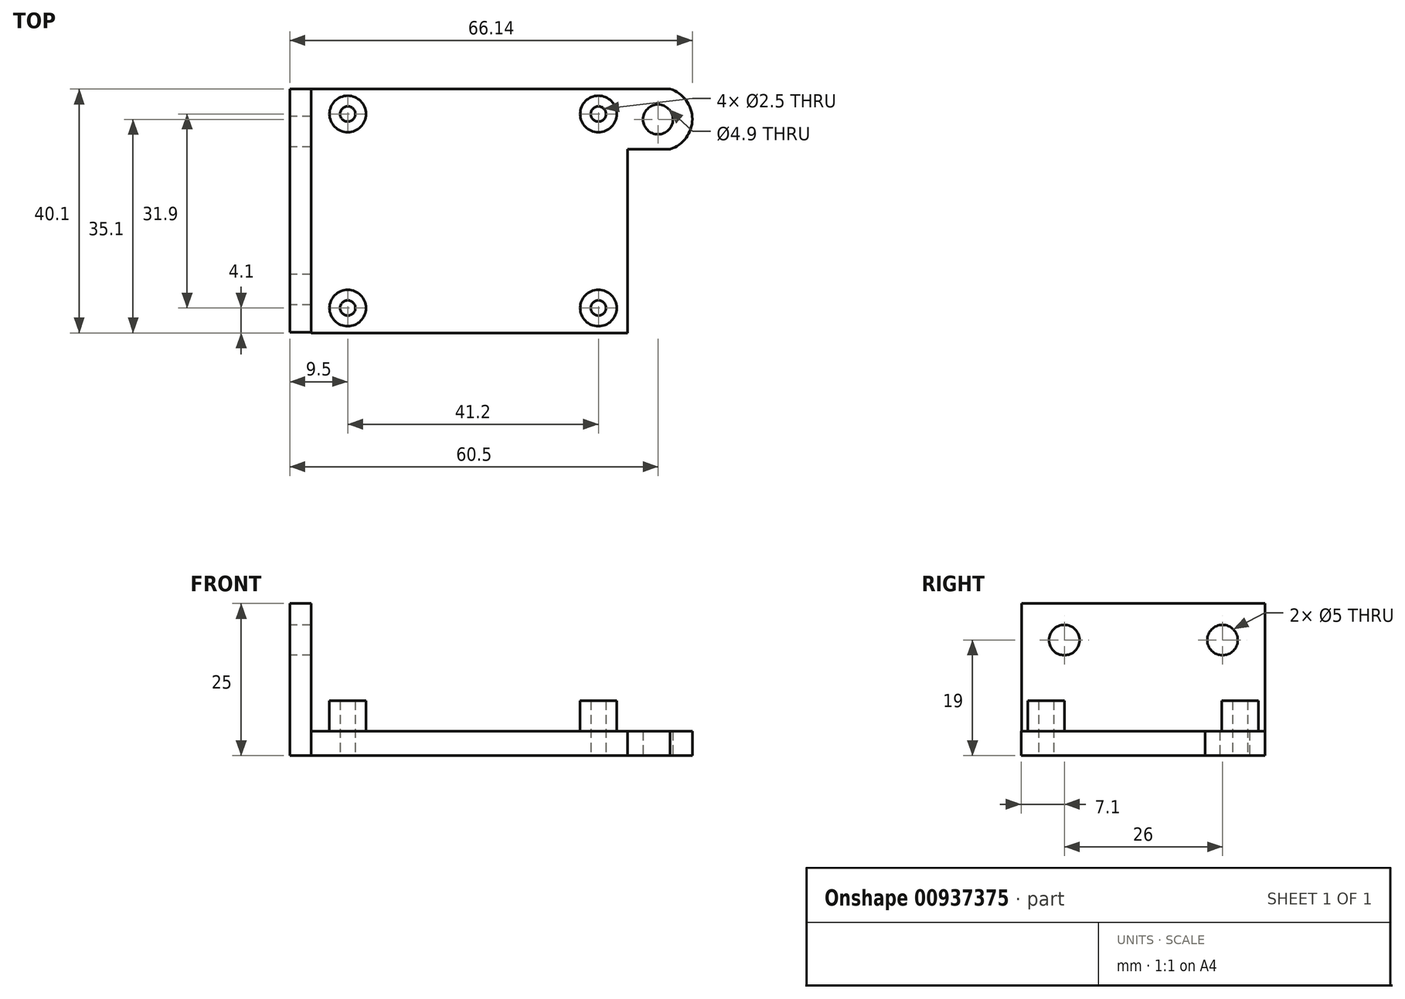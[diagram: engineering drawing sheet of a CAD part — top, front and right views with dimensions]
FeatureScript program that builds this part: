
annotation { "Feature Type Name" : "Feature", "Feature Type Description" : "" }
export const myFeature = defineFeature(function(context is Context, id is Id, definition is map)
    precondition{}
    {
        {
            var Q0;
            Q0=qCreatedBy(makeId("Top.planeOp"),FACE);
            var sketch = newSketch(context, id + "F0", { "sketchPlane" : qUnion([Q0])});
            skLineSegment(sketch, "E0", {"start": v(0, 20) * mm, "end": v(0, -41.37) * mm, "construction": true});
            skLineSegment(sketch, "E1", {"start": v(-1.26, 0) * mm, "end": v(38.44, 0) * mm, "construction": true});
            skLineSegment(sketch, "E2", {"start": v(0, 20) * mm, "end": v(0, -20) * mm});
            skLineSegment(sketch, "E3", {"start": v(0, -20) * mm, "end": v(3.5, -20) * mm});
            skLineSegment(sketch, "E4", {"start": v(3.5, -20) * mm, "end": v(3.5, 20) * mm});
            skLineSegment(sketch, "E5", {"start": v(0, 20) * mm, "end": v(3.5, 20) * mm});
            skLineSegment(sketch, "E6.bottom", {"start": v(3.5, 20) * mm, "end": v(54.6, 20) * mm});
            skLineSegment(sketch, "E6.top", {"start": v(3.5, -20.1) * mm, "end": v(55.5, -20.1) * mm});
            skLineSegment(sketch, "E6.left", {"start": v(3.5, 20) * mm, "end": v(3.5, -20.1) * mm});
            skLineSegment(sketch, "E7", {"start": v(-2.6, 15.9) * mm, "end": v(69.6, 15.9) * mm, "construction": true});
            skLineSegment(sketch, "E8", {"start": v(-2.04, -16) * mm, "end": v(63.55, -16) * mm, "construction": true});
            skLineSegment(sketch, "E9", {"start": v(50.7, 23.58) * mm, "end": v(50.7, -20.6) * mm, "construction": true});
            skLineSegment(sketch, "E10", {"start": v(9.5, 22.43) * mm, "end": v(9.5, -22.92) * mm, "construction": true});
            skCircle(sketch, "E11", {"center": v(9.5, 15.9) * mm, "radius": 1.25 * mm});
            skCircle(sketch, "E12", {"center": v(9.5, 15.9) * mm, "radius": 3 * mm});
            skCircle(sketch, "E13", {"center": v(9.5, -16) * mm, "radius": 1.25 * mm});
            skCircle(sketch, "E14", {"center": v(9.5, -16) * mm, "radius": 3 * mm});
            skCircle(sketch, "E15", {"center": v(50.7, -16) * mm, "radius": 1.25 * mm});
            skCircle(sketch, "E16", {"center": v(50.7, -16) * mm, "radius": 3 * mm});
            skCircle(sketch, "E17", {"center": v(50.7, 15.9) * mm, "radius": 1.25 * mm});
            skCircle(sketch, "E18", {"center": v(50.7, 15.9) * mm, "radius": 3 * mm});
            skLineSegment(sketch, "E19.bottom", {"start": v(54.6, 20) * mm, "end": v(62.5, 20) * mm});
            skLineSegment(sketch, "E19.top", {"start": v(55.5, 10.12) * mm, "end": v(62.5, 10.12) * mm});
            skLineSegment(sketch, "E20.trimOffspring", {"start": v(55.5, 10.12) * mm, "end": v(55.5, -20.1) * mm});
            skCircle(sketch, "E21", {"center": v(60.5, 15) * mm, "radius": 2.45 * mm});
            skArc(sketch, "E22", {"start": v(62.5, 10.12) * mm, "mid": v(66.14, 15.06) * mm, "end": v(62.5, 20) * mm});
            skLineSegment(sketch, "E23", {"start": v(62.5, 20) * mm, "end": v(62.5, 7.04) * mm, "construction": true});
            skPoint(sketch, "E19.right.start.orphan", {"position": v(74.83, 20) * mm});
            skSolve(sketch);
        }
        {
            var Q0;
            Q0=makeQuery(id+"F0.imprint","IMPRINT",FACE,{"disambiguationData":[TD([[makeQuery(id+"F0.imprint","IMPRINT",EDGE,{"derivedFrom":sQuery(id+"F0.wireOp",EDGE,"E4")}),-1.0]])]});
            extrude(context, id + "F1", {"entities" : qUnion([Q0]), "depth" : 4 * mm, "offsetDistance" : 25 * mm});
        }
        {
            var Q0;
            Q0=makeQuery(id+"F0.imprint","IMPRINT",FACE,{"disambiguationData":[TD([[makeQuery(id+"F0.imprint","IMPRINT",EDGE,{"derivedFrom":sQuery(id+"F0.wireOp",EDGE,"E11")}),-1.0]])]});
            var Q1;
            Q1=makeQuery(id+"F0.imprint","IMPRINT",FACE,{"disambiguationData":[TD([[makeQuery(id+"F0.imprint","IMPRINT",EDGE,{"derivedFrom":sQuery(id+"F0.wireOp",EDGE,"E17")}),-1.0]])]});
            var Q2;
            Q2=makeQuery(id+"F0.imprint","IMPRINT",FACE,{"disambiguationData":[TD([[makeQuery(id+"F0.imprint","IMPRINT",EDGE,{"derivedFrom":sQuery(id+"F0.wireOp",EDGE,"E15")}),-1.0]])]});
            var Q3;
            Q3=makeQuery(id+"F0.imprint","IMPRINT",FACE,{"disambiguationData":[TD([[makeQuery(id+"F0.imprint","IMPRINT",EDGE,{"derivedFrom":sQuery(id+"F0.wireOp",EDGE,"E13")}),-1.0]])]});
            extrude(context, id + "F2", {"entities" : qUnion([Q0, Q1, Q2, Q3]), "operationType" : NewBodyOperationType.ADD, "depth" : 9 * mm, "offsetDistance" : 25 * mm});
        }
        {
            var Q0;
            Q0=makeQuery(id+"F0.imprint","IMPRINT",FACE,{"disambiguationData":[TD([[makeQuery(id+"F0.imprint","IMPRINT",EDGE,{"derivedFrom":sQuery(id+"F0.wireOp",EDGE,"E2")}),1.0]])]});
            extrude(context, id + "F3", {"entities" : qUnion([Q0]), "operationType" : NewBodyOperationType.ADD, "depth" : 25 * mm, "offsetDistance" : 25 * mm});
        }
        {
            var Q0;
            Q0=qCreatedBy(makeId("Right.planeOp"),FACE);
            var sketch = newSketch(context, id + "F4", { "sketchPlane" : qUnion([Q0])});
            skLineSegment(sketch, "E24", {"start": v(17.4, 19) * mm, "end": v(-20.68, 19) * mm, "construction": true});
            skLineSegment(sketch, "E25", {"start": v(18.22, 0) * mm, "end": v(-21.5, 0) * mm, "construction": true});
            skLineSegment(sketch, "E26", {"start": v(-20, 29.44) * mm, "end": v(-20, -5.39) * mm, "construction": true});
            skLineSegment(sketch, "E27", {"start": v(-13, 28.52) * mm, "end": v(-13, 12.37) * mm, "construction": true});
            skLineSegment(sketch, "E28", {"start": v(13, 26.84) * mm, "end": v(13, 12.37) * mm, "construction": true});
            skCircle(sketch, "E29", {"center": v(13, 19) * mm, "radius": 2.5 * mm});
            skCircle(sketch, "E30", {"center": v(-13, 19) * mm, "radius": 2.5 * mm});
            skSolve(sketch);
        }
        {
            var Q0;
            Q0 = qSketchRegion(id + "F4", true);
            extrude(context, id + "F5", {"entities" : qUnion([Q0]), "operationType" : NewBodyOperationType.REMOVE, "depth" : 25 * mm, "offsetDistance" : 25 * mm});
        }
    });
